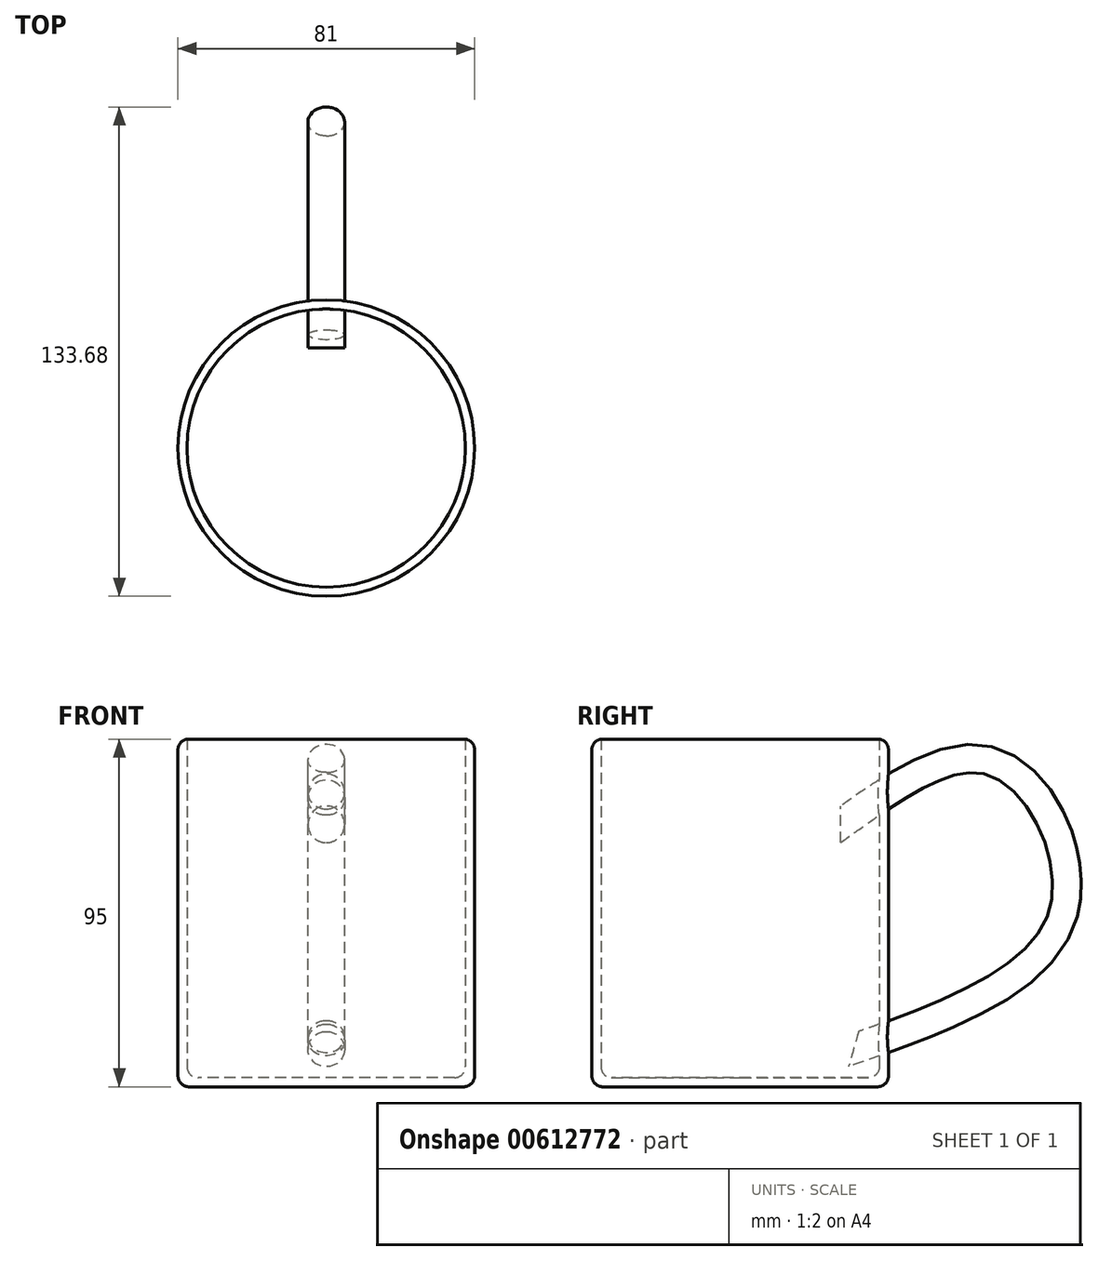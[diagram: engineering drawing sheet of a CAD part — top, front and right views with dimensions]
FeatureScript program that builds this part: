
annotation { "Feature Type Name" : "Feature", "Feature Type Description" : "" }
export const myFeature = defineFeature(function(context is Context, id is Id, definition is map)
    precondition{}
    {
        {
            var Q0;
            Q0=qCreatedBy(makeId("Top.planeOp"),FACE);
            var sketch = newSketch(context, id + "F0", { "sketchPlane" : qUnion([Q0])});
            skCircle(sketch, "E0", {"center": v(0, 0) * mm, "radius": 40.5 * mm});
            skSolve(sketch);
        }
        {
            var Q0;
            Q0 = qSketchRegion(id + "F0", true);
            extrude(context, id + "F1", {"entities" : qUnion([Q0]), "depth" : 95 * mm, "offsetDistance" : 25 * mm});
        }
        {
            var Q0;
            Q0=makeQuery(id+"F1.opExtrude","CAP_FACE",FACE,{"disambiguationData":[OSD([sQuery(id+"F0.wireOp",EDGE,"E0")])],"isStart":false});
            shell(context, id + "F2", {"entities" : qUnion([Q0]), "thickness" : 2.5 * mm});
        }
        {
            var Q0;
            Q0=qCreatedBy(makeId("Right.planeOp"),FACE);
            var sketch = newSketch(context, id + "F3", { "sketchPlane" : qUnion([Q0])});
            skFitSpline(sketch, "E1", {"points": [v(29.5, 70.79) * mm, v(69.86, 86.15) * mm, v(86.13, 47.9) * mm, v(29.2, 11.74) * mm], "startDerivative": vector(139.13, 98.42) * mm, "endDerivative": vector(-201.03, -70.94) * mm});
            skSolve(sketch);
        }
        {
            var Q0;
            Q0=qCreatedBy(makeId("Front.planeOp"),FACE);
            cPlane(context, id + "F4", {"entities" : qUnion([Q0]), "cplaneType" : CPlaneType.OFFSET, "offset" : 27.4 * mm, "oppositeDirection" : true, "width" : 150 * mm, "height" : 150 * mm});
        }
        {
            var Q0;
            Q0=qCreatedBy(id+"F4.planeOp",FACE);
            var sketch = newSketch(context, id + "F5", { "sketchPlane" : qUnion([Q0])});
            skCircle(sketch, "E2", {"center": v(0, 71.7) * mm, "radius": 5 * mm});
            skSolve(sketch);
        }
        {
            var Q0;
            Q0 = qSketchRegion(id + "F5", true);
            var Q1;
            Q1=sQuery(id+"F3.wireOp",EDGE,"E1");
            sweep(context, id + "F6", {"operationType" : NewBodyOperationType.ADD, "profiles" : qUnion([Q0]), "path" : qUnion([Q1])});
        }
        {
            var Q0;
            Q0=makeQuery(id+"F1.opExtrude","CAP_EDGE",EDGE,{"disambiguationData":[OSD([sQuery(id+"F0.wireOp",EDGE,"E0")])],"isStart":false});
            var Q1;
            {var subQ0=sQuery(id+"F0.wireOp",EDGE,"E0");Q1=makeQuery(id+"F2.opShell","OFFSET_EDGE",EDGE,{"disambiguationData":[OSD([subQ0]),TDD([makeQuery(id+"F1.opExtrude","CAP_EDGE",EDGE,{"disambiguationData":[OSD([subQ0])],"isStart":true})])]});}
            var Q2;
            Q2=makeQuery(id+"F1.opExtrude","CAP_EDGE",EDGE,{"disambiguationData":[OSD([sQuery(id+"F0.wireOp",EDGE,"E0")])],"isStart":true});
            fillet(context, id + "F7", {"entities" : qUnion([Q0, Q1, Q2]), "radius" : 3 * mm, "tangentPropagation" : true, "allowEdgeOverflow" : false});
        }
    });
